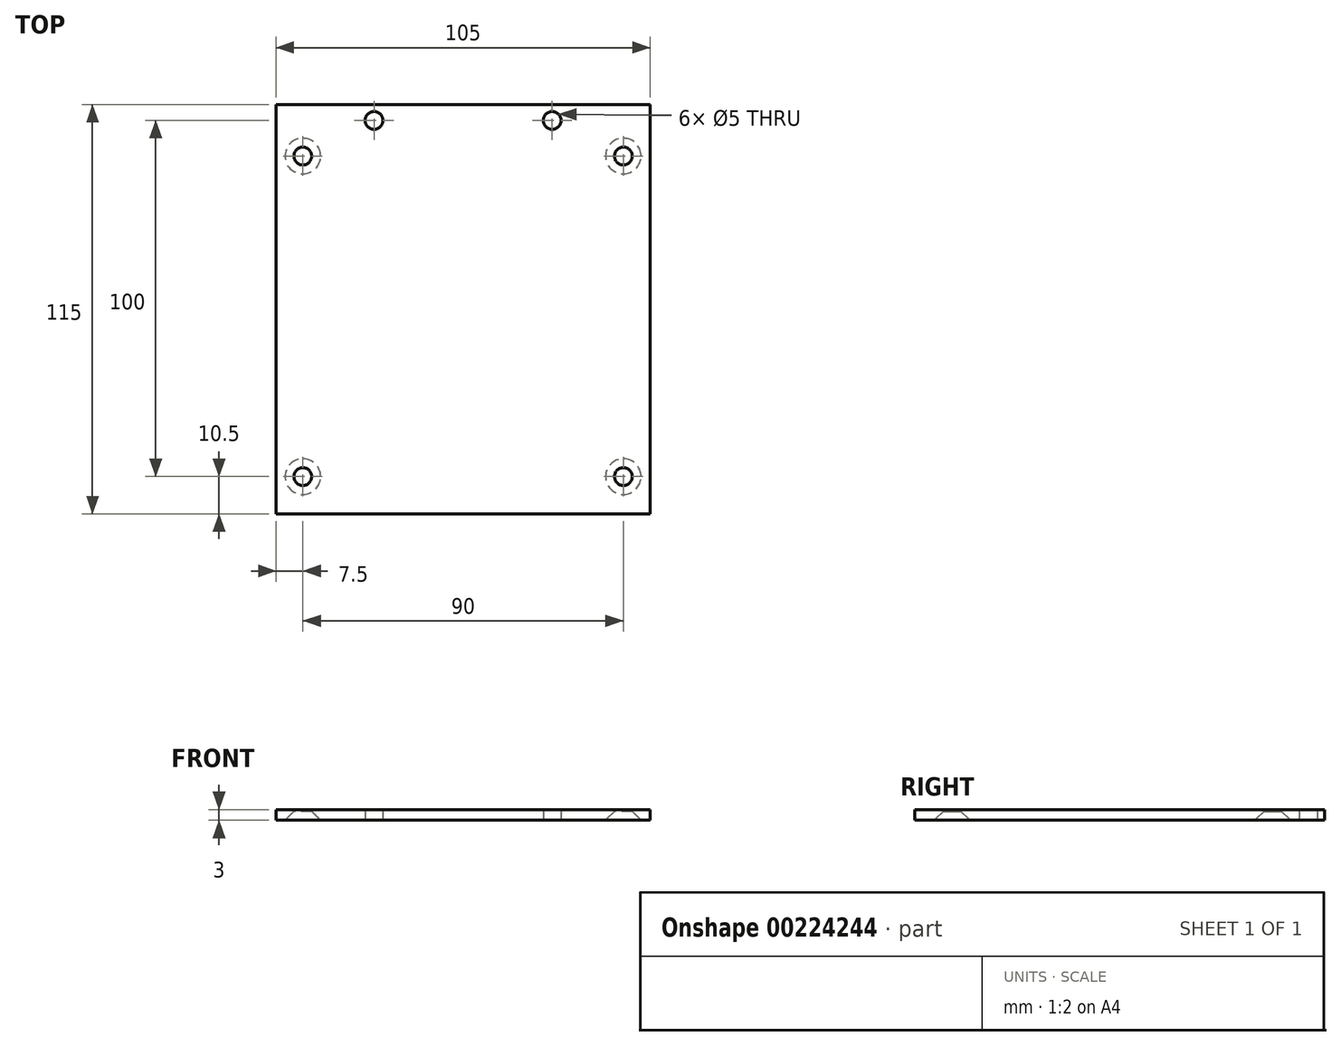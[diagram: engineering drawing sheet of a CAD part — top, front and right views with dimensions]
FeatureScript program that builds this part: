
annotation { "Feature Type Name" : "Feature", "Feature Type Description" : "" }
export const myFeature = defineFeature(function(context is Context, id is Id, definition is map)
    precondition{}
    {
        {
            var Q0;
            Q0=qCreatedBy(makeId("Top.planeOp"),FACE);
            var sketch = newSketch(context, id + "F0", { "sketchPlane" : qUnion([Q0])});
            skLineSegment(sketch, "E0.bottom", {"start": v(52.5, 59.5) * mm, "end": v(-52.5, 59.5) * mm});
            skLineSegment(sketch, "E0.top", {"start": v(52.5, -55.5) * mm, "end": v(-52.5, -55.5) * mm});
            skLineSegment(sketch, "E0.left", {"start": v(52.5, 59.5) * mm, "end": v(52.5, -55.5) * mm});
            skLineSegment(sketch, "E0.right", {"start": v(-52.5, 59.5) * mm, "end": v(-52.5, -55.5) * mm});
            skPoint(sketch, "E0.middle", {"position": v(0, 0) * mm});
            skCircle(sketch, "E1", {"center": v(25, 55) * mm, "radius": 2.5 * mm});
            skCircle(sketch, "E2", {"center": v(-25, 55) * mm, "radius": 2.5 * mm});
            skCircle(sketch, "E3", {"center": v(-45, 45) * mm, "radius": 2.5 * mm});
            skCircle(sketch, "E4", {"center": v(45, 45) * mm, "radius": 2.5 * mm});
            skCircle(sketch, "E5", {"center": v(45, -45) * mm, "radius": 2.5 * mm});
            skCircle(sketch, "E6", {"center": v(-45, -45) * mm, "radius": 2.5 * mm});
            skSolve(sketch);
        }
        {
            var Q0;
            Q0=makeQuery(id+"F0.imprint","IMPRINT",FACE,{"disambiguationData":[TD([[makeQuery(id+"F0.imprint","IMPRINT",EDGE,{"derivedFrom":sQuery(id+"F0.wireOp",EDGE,"E0.bottom")}),1.0]])]});
            extrude(context, id + "F1", {"entities" : qUnion([Q0]), "depth" : 3 * mm});
        }
        {
            var Q0;
            Q0=makeQuery(id+"F1.opExtrude","CAP_EDGE",EDGE,{"disambiguationData":[OSD([sQuery(id+"F0.wireOp",EDGE,"E6")])],"isStart":true});
            var Q1;
            Q1=makeQuery(id+"F1.opExtrude","CAP_EDGE",EDGE,{"disambiguationData":[OSD([sQuery(id+"F0.wireOp",EDGE,"E5")])],"isStart":true});
            var Q2;
            Q2=makeQuery(id+"F1.opExtrude","CAP_EDGE",EDGE,{"disambiguationData":[OSD([sQuery(id+"F0.wireOp",EDGE,"E4")])],"isStart":true});
            var Q3;
            Q3=makeQuery(id+"F1.opExtrude","CAP_EDGE",EDGE,{"disambiguationData":[OSD([sQuery(id+"F0.wireOp",EDGE,"E3")])],"isStart":true});
            chamfer(context, id + "F2", {"entities" : qUnion([Q0, Q1, Q2, Q3]), "chamferType" : ChamferType.OFFSET_ANGLE, "width" : 2.5 * mm, "oppositeDirection" : false, "angle" : 45 * degree, "tangentPropagation" : true});
        }
    });
